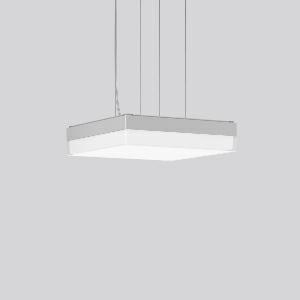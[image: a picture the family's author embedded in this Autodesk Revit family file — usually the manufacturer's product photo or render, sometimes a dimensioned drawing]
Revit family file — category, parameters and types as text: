
# Revit family: flat_slim_square_312542_004_6856
name_source: partatom
category: Lighting Fixtures
units: mm (PartAtom-declared; Revit-internal decimal feet)

## family parameters
Cut with Voids When Loaded = No
Host = Face
Light Source = No
Part Type = Normal
Room Calculation Point = No
Round Connector Dimension = Use Diameter
Shared = No

## types (1)
- MultiLumen 2 840 (1 x LED Modul 840, 2200 lm, 4000)
    Apparent Load = 19 VA
    CIE Flux Codes = 43 75 93 91 100
    Color Rendering = 80
    Color Temperature = 4000
    Default Elevation = 1800 mm
    Height = 70 mm
    Lamp = 1 x LED Modul 840
    Lamp Light Flux = 2200 lm
    Lamp count = 1
    Length = 300 mm
    Lifetime = 50000 h
    Luminous efficacy = 116 lm/W
    Manufacturer = RZB
    ModVariant = No
    Model = 312542.004
    Mounting Place = Ceiling
    Mounting Type = Pendant
    Number of Poles = 1
    OnlyDefault = Yes
    Power Factor = 1
    Product Name = FLAT SLIM square
    Product group = Pendant luminaires
    ProductGroupID = 902
    Protection Class = Protection class I
    Protection Degree = IP 40
    RLX_Detail_Level = 1
    RLX_Emergency_Light_Flux = 0 lm
    RLX_Emergency_Type = 0
    RLX_Emergency_Type_DB = No
    RlxData = <blob elided: 14289 chars, md5=38f078e6>
    Socket = socket
    Standby Power = 0 W
    System Light Flux = 2200 lm
    System Power = 19 W
    Type Comments = MultiLumen 2 840
    Type Image = 312542.004.jpg
    URL = http://relux.com
    VarID = multilumen_2_840
    Voltage = 230 V
    Voltage Range = 220-240 V
    Weight = 0.00 kg
    Width = 300 mm

## geometry (parser evidence)
native form markers: Sweep x15
no freeform markers — native parametric forms only
